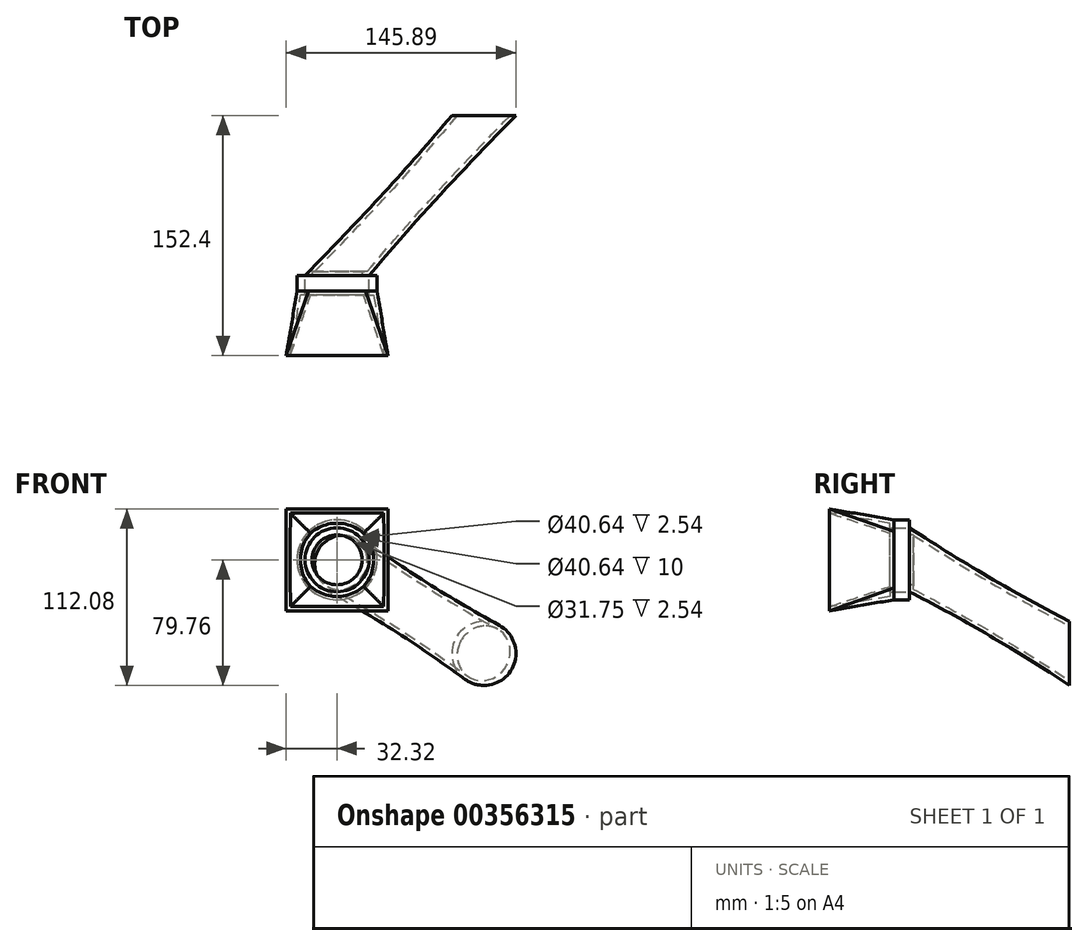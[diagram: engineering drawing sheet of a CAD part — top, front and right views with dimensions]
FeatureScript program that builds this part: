
annotation { "Feature Type Name" : "Feature", "Feature Type Description" : "" }
export const myFeature = defineFeature(function(context is Context, id is Id, definition is map)
    precondition{}
    {
        {
            var Q0;
            Q0=qCreatedBy(makeId("Front.planeOp"),FACE);
            var sketch = newSketch(context, id + "F0", { "sketchPlane" : qUnion([Q0])});
            skCircle(sketch, "E0", {"center": v(0, 0) * mm, "radius": 20.32 * mm});
            skCircle(sketch, "E1", {"center": v(0, 0) * mm, "radius": 25.4 * mm});
            skSolve(sketch);
        }
        {
            var Q0;
            Q0 = qSketchRegion(id + "F0", true);
            var Q1;
            Q1 = qSketchRegion(id + "F3", true);
            extrude(context, id + "F1", {"entities" : qUnion([Q0, Q1]), "depth" : 10 * mm});
        }
        {
            var Q0;
            Q0=qCreatedBy(makeId("Front.planeOp"),FACE);
            cPlane(context, id + "F2", {"entities" : qUnion([Q0]), "cplaneType" : CPlaneType.OFFSET, "offset" : 50.8 * mm, "width" : 152.4 * mm, "height" : 152.4 * mm});
        }
        {
            var Q0;
            Q0=qCreatedBy(id+"F2.planeOp",FACE);
            var sketch = newSketch(context, id + "F3", { "sketchPlane" : qUnion([Q0])});
            skLineSegment(sketch, "E2.bottom", {"start": v(-32.32, 32.32) * mm, "end": v(32.32, 32.32) * mm});
            skLineSegment(sketch, "E2.top", {"start": v(-32.32, -32.32) * mm, "end": v(32.32, -32.32) * mm});
            skLineSegment(sketch, "E2.left", {"start": v(-32.32, 32.32) * mm, "end": v(-32.32, -32.32) * mm});
            skLineSegment(sketch, "E2.right", {"start": v(32.32, 32.32) * mm, "end": v(32.32, -32.32) * mm});
            skPoint(sketch, "E3.startSnap0", {"position": v(0, -32.32) * mm});
            skSolve(sketch);
        }
        {
            var Q0;
            Q0=makeQuery(id+"F1.opExtrude","CAP_FACE",FACE,{"disambiguationData":[OSD([sQuery(id+"F0.wireOp",EDGE,"E0"),sQuery(id+"F0.wireOp",EDGE,"E1")])],"isStart":false});
            cPlane(context, id + "F4", {"entities" : qUnion([Q0]), "cplaneType" : CPlaneType.OFFSET, "offset" : 0 * mm, "width" : 152.4 * mm, "height" : 152.4 * mm});
        }
        {
            var Q0;
            Q0=qCreatedBy(id+"F4.planeOp",FACE);
            var sketch = newSketch(context, id + "F5", { "sketchPlane" : qUnion([Q0])});
            skCircle(sketch, "E4.0", {"center": v(0, 0) * mm, "radius": 25.4 * mm});
            skSolve(sketch);
        }
        {
            var Q0;
            Q0 = qSketchRegion(id + "F3", true);
            var Q1;
            Q1 = qSketchRegion(id + "F5", true);
            var Q2;
            Q2 = qConstructionFilter(qBodyType(qCreatedBy(id + "F3" ,EDGE), BodyType.WIRE), ConstructionObject.NO);
            var Q3;
            Q3 = qConstructionFilter(qBodyType(qCreatedBy(id + "F5" ,EDGE), BodyType.WIRE), ConstructionObject.NO);
            loft(context, id + "F6", {"sheetProfilesArray" : [{ "sheetProfileEntities" : qUnion([Q0]) }, { "sheetProfileEntities" : qUnion([Q1]) }], "wireProfilesArray" : [{ "wireProfileEntities" : qUnion([Q2]) }, { "wireProfileEntities" : qUnion([Q3]) }]});
        }
        {
            var Q0;
            Q0=makeQuery(id+"F6.opLoft","CAP_FACE",FACE,{"disambiguationData":[OSD([makeQuery(id+"F3.imprint","IMPRINT",FACE,{"disambiguationData":[TD([[makeQuery(id+"F3.imprint","IMPRINT",EDGE,{"derivedFrom":sQuery(id+"F3.wireOp",EDGE,"E2.bottom")}),-1.0]])]})])],"isStart":true});
            var Q1;
            Q1=makeQuery(id+"F6.opLoft","SWEPT_BODY",BODY,{"disambiguationData":[OSD([makeQuery(id+"F3.imprint","IMPRINT",FACE,{"disambiguationData":[TD([[makeQuery(id+"F3.imprint","IMPRINT",EDGE,{"derivedFrom":sQuery(id+"F3.wireOp",EDGE,"E2.bottom")}),-1.0]])]}),makeQuery(id+"F5.imprint","IMPRINT",FACE,{"disambiguationData":[TD([[makeQuery(id+"F5.imprint","IMPRINT",EDGE,{"derivedFrom":sQuery(id+"F5.wireOp",EDGE,"E4.0")}),1.0]])]})])]});
            shell(context, id + "F7", {"entities" : qUnion([Q0]), "parts" : qUnion([Q1]), "thickness" : 2.54 * mm});
        }
        {
            var Q0;
            Q0=qCreatedBy(id+"F4.planeOp",FACE);
            var sketch = newSketch(context, id + "F8", { "sketchPlane" : qUnion([Q0])});
            skCircle(sketch, "E5.0", {"center": v(0, 0) * mm, "radius": 20.32 * mm});
            skSolve(sketch);
        }
        {
            var Q0;
            Q0 = qSketchRegion(id + "F8", true);
            extrude(context, id + "F9", {"entities" : qUnion([Q0]), "operationType" : NewBodyOperationType.REMOVE, "endBound" : BoundingType.THROUGH_ALL, "depth" : 25.4 * mm});
        }
        {
            var Q0;
            Q0=qCreatedBy(makeId("Front.planeOp"),FACE);
            cPlane(context, id + "F10", {"entities" : qUnion([Q0]), "cplaneType" : CPlaneType.OFFSET, "offset" : 101.6 * mm, "oppositeDirection" : true, "width" : 152.4 * mm, "height" : 152.4 * mm});
        }
        {
            var Q0;
            Q0=qCreatedBy(id+"F10.planeOp",FACE);
            var sketch = newSketch(context, id + "F11", { "sketchPlane" : qUnion([Q0])});
            skCircle(sketch, "E6", {"center": v(93.25, -59.44) * mm, "radius": 25.4 * mm});
            skCircle(sketch, "E7", {"center": v(93.25, -59.44) * mm, "radius": 20.32 * mm});
            skSolve(sketch);
        }
        {
            var Q0;
            Q0=makeQuery(id+"F11.imprint","IMPRINT",FACE,{"disambiguationData":[TD([[makeQuery(id+"F11.imprint","IMPRINT",EDGE,{"derivedFrom":sQuery(id+"F11.wireOp",EDGE,"E7")}),1.0]])]});
            var Q1;
            Q1=makeQuery(id+"F0.imprint","IMPRINT",FACE,{"disambiguationData":[TD([[makeQuery(id+"F0.imprint","IMPRINT",EDGE,{"derivedFrom":sQuery(id+"F0.wireOp",EDGE,"E0")}),1.0]])]});
            loft(context, id + "F12", {"sheetProfilesArray" : [{ "sheetProfileEntities" : qUnion([Q0]) }, { "sheetProfileEntities" : qUnion([Q1]) }]});
        }
        {
            var Q0;
            Q0=makeQuery(id+"F12.opLoft","CAP_FACE",FACE,{"disambiguationData":[OSD([makeQuery(id+"F11.imprint","IMPRINT",FACE,{"disambiguationData":[TD([[makeQuery(id+"F11.imprint","IMPRINT",EDGE,{"derivedFrom":sQuery(id+"F11.wireOp",EDGE,"E7")}),1.0]])]})])],"isStart":true});
            shell(context, id + "F13", {"entities" : qUnion([Q0]), "thickness" : 2.54 * mm});
        }
        {
            var Q0;
            Q0=qCreatedBy(makeId("Front.planeOp"),FACE);
            var sketch = newSketch(context, id + "F14", { "sketchPlane" : qUnion([Q0])});
            skCircle(sketch, "E8", {"center": v(0, 0) * mm, "radius": 15.88 * mm});
            skSolve(sketch);
        }
        {
            var Q0;
            Q0 = qSketchRegion(id + "F14", true);
            extrude(context, id + "F15", {"entities" : qUnion([Q0]), "operationType" : NewBodyOperationType.REMOVE, "oppositeDirection" : true, "depth" : 2.54 * mm});
        }
    });
